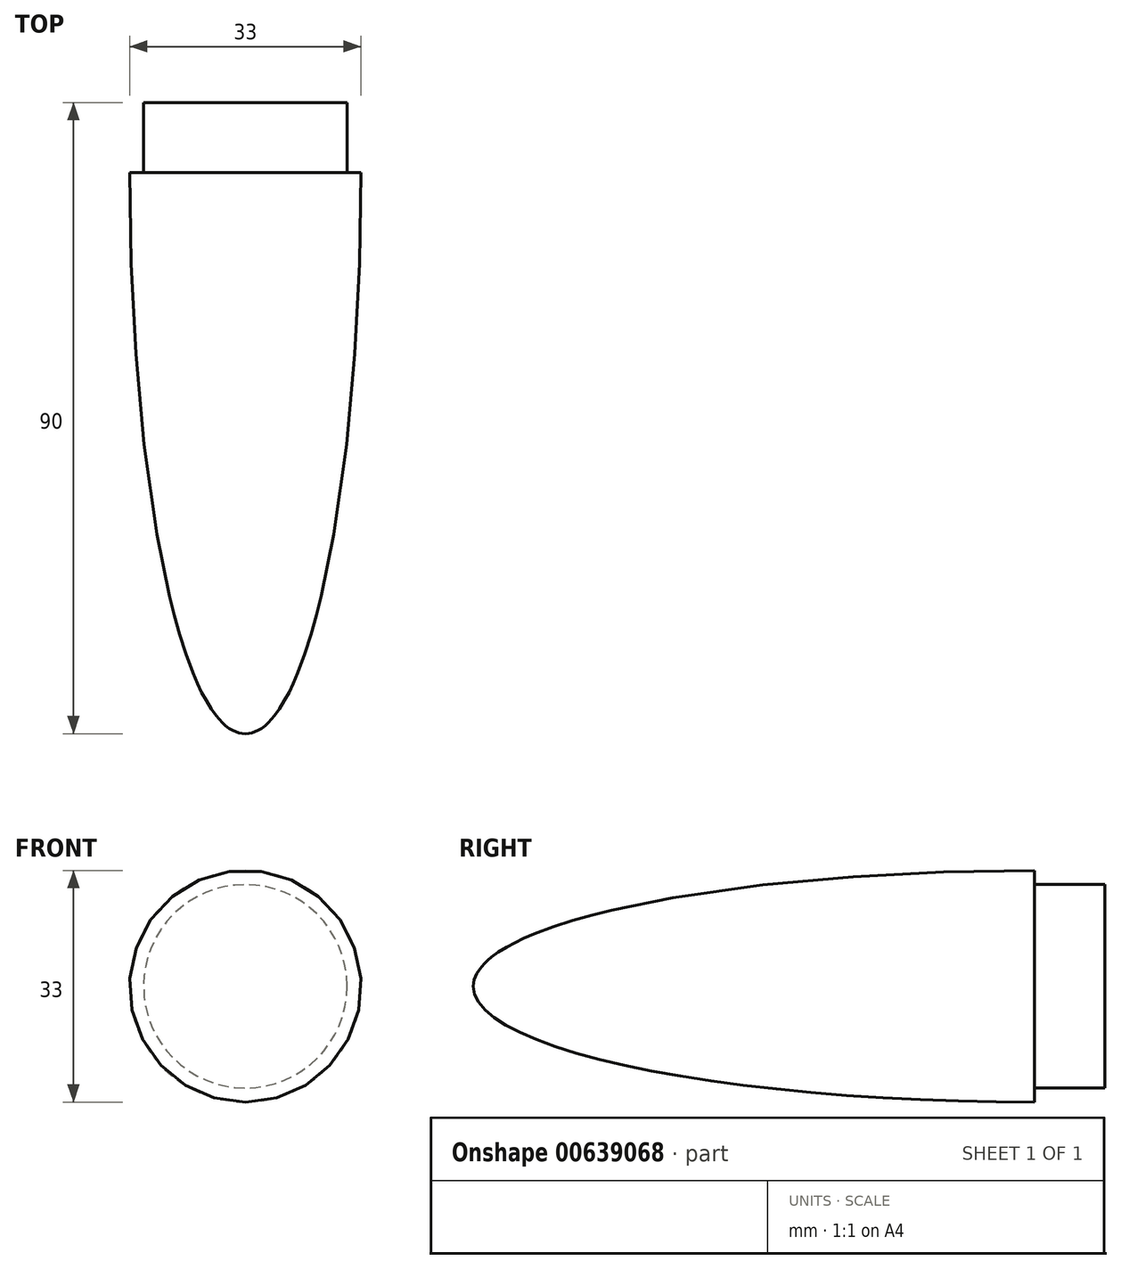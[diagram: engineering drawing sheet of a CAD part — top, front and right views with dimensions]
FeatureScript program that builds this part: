
annotation { "Feature Type Name" : "Feature", "Feature Type Description" : "" }
export const myFeature = defineFeature(function(context is Context, id is Id, definition is map)
    precondition{}
    {
        {
            var Q0;
            Q0=qCreatedBy(makeId("Right.planeOp"),FACE);
            var sketch = newSketch(context, id + "F0", { "sketchPlane" : qUnion([Q0])});
            skLineSegment(sketch, "E0.bottom", {"start": v(0, 0) * mm, "end": v(10, 0) * mm});
            skLineSegment(sketch, "E0.top", {"start": v(0, -14.5) * mm, "end": v(10, -14.5) * mm});
            skLineSegment(sketch, "E0.left", {"start": v(0, 0) * mm, "end": v(0, -14.5) * mm});
            skLineSegment(sketch, "E0.right", {"start": v(10, 0) * mm, "end": v(10, -14.5) * mm});
            skLineSegment(sketch, "E1.bottom", {"start": v(0, 0) * mm, "end": v(-80, 0) * mm});
            skLineSegment(sketch, "E1.top", {"start": v(0, -16.5) * mm, "end": v(-80, -16.5) * mm});
            skLineSegment(sketch, "E1.left", {"start": v(0, 0) * mm, "end": v(0, -16.5) * mm});
            skLineSegment(sketch, "E1.right", {"start": v(-80, 0) * mm, "end": v(-80, -16.5) * mm});
            skEllipse(sketch, "E2", {"center": v(0, 0) * mm, "majorRadius": 80 * mm, "minorRadius": 16.5 * mm, "majorAxis": v(-1, 0)});
            skSolve(sketch);
        }
        {
            var Q0;
            {var subQ0=sQuery(id+"F0.wireOp",EDGE,"E1.bottom");Q0=makeQuery(id+"F0.imprint","IMPRINT",FACE,{"disambiguationData":[TD([[makeQuery(id+"F0.imprint","IMPRINT",EDGE,{"derivedFrom":subQ0}),1.0]])]});}
            var Q1;
            {var subQ0=sQuery(id+"F0.wireOp",EDGE,"E0.bottom");Q1=makeQuery(id+"F0.imprint","IMPRINT",FACE,{"disambiguationData":[TD([[makeQuery(id+"F0.imprint","IMPRINT",EDGE,{"derivedFrom":subQ0}),-1.0]])]});}
            var Q2;
            Q2=sQuery(id+"F0.wireOp",EDGE,"E1.bottom");
            revolve(context, id + "F1", {"entities" : qUnion([Q0, Q1]), "axis" : qUnion([Q2]), "revolveType" : RevolveType.FULL});
        }
    });
